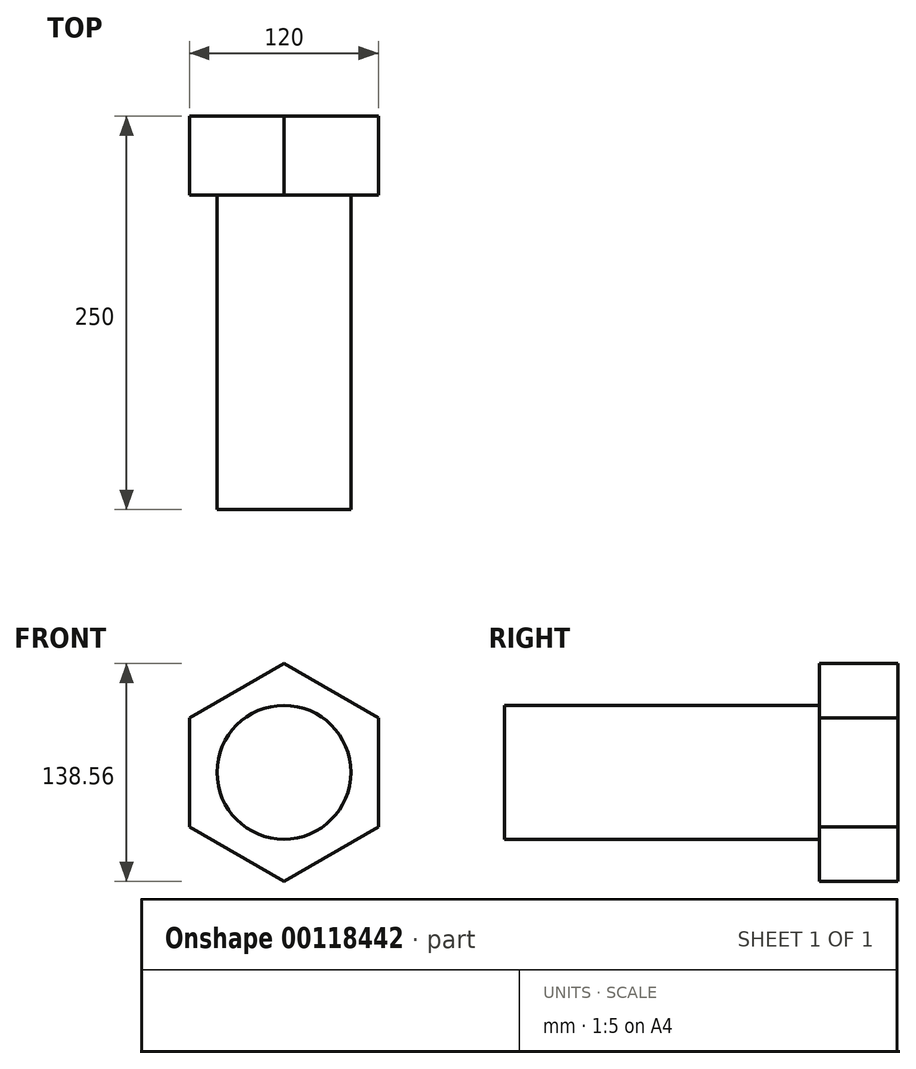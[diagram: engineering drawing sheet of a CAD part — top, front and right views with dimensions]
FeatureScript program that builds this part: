
annotation { "Feature Type Name" : "Feature", "Feature Type Description" : "" }
export const myFeature = defineFeature(function(context is Context, id is Id, definition is map)
    precondition{}
    {
        {
            var Q0;
            Q0=qCreatedBy(makeId("Front.planeOp"),FACE);
            var sketch = newSketch(context, id + "F0", { "sketchPlane" : qUnion([Q0])});
            skCircle(sketch, "E0.cCircle", {"center": v(0, 0) * mm, "radius": 60 * mm, "construction": true});
            skLineSegment(sketch, "E0.0", {"start": v(-60, -34.64) * mm, "end": v(-60, 34.64) * mm});
            skLineSegment(sketch, "E0.1", {"start": v(-60, 34.64) * mm, "end": v(0, 69.28) * mm});
            skLineSegment(sketch, "E0.2", {"start": v(0, 69.28) * mm, "end": v(60, 34.64) * mm});
            skLineSegment(sketch, "E0.3", {"start": v(60, 34.64) * mm, "end": v(60, -34.64) * mm});
            skLineSegment(sketch, "E0.4", {"start": v(60, -34.64) * mm, "end": v(0, -69.28) * mm});
            skLineSegment(sketch, "E0.5", {"start": v(0, -69.28) * mm, "end": v(-60, -34.64) * mm});
            skPoint(sketch, "E0.0.midPoint", {"position": v(-60, 0) * mm});
            skSolve(sketch);
        }
        {
            var Q0;
            Q0 = qSketchRegion(id + "F0", true);
            extrude(context, id + "F1", {"entities" : qUnion([Q0]), "endBound" : BoundingType.SYMMETRIC, "depth" : 50 * mm});
        }
        {
            var Q0;
            Q0=makeQuery(id+"F1.opExtrude","CAP_FACE",FACE,{"disambiguationData":[OSD([sQuery(id+"F0.wireOp",EDGE,"E0.0"),sQuery(id+"F0.wireOp",EDGE,"E0.1"),sQuery(id+"F0.wireOp",EDGE,"E0.2"),sQuery(id+"F0.wireOp",EDGE,"E0.3"),sQuery(id+"F0.wireOp",EDGE,"E0.4"),sQuery(id+"F0.wireOp",EDGE,"E0.5")])],"isStart":false});
            var sketch = newSketch(context, id + "F2", { "sketchPlane" : qUnion([Q0])});
            skCircle(sketch, "E1", {"center": v(0, 0) * mm, "radius": 42.5 * mm});
            skSolve(sketch);
        }
        {
            var Q0;
            Q0=makeQuery(id+"F2.imprint","IMPRINT",FACE,{"disambiguationData":[TD([[makeQuery(id+"F2.imprint","IMPRINT",EDGE,{"derivedFrom":sQuery(id+"F2.wireOp",EDGE,"E1")}),1.0]])]});
            extrude(context, id + "F3", {"entities" : qUnion([Q0]), "operationType" : NewBodyOperationType.ADD, "depth" : 200 * mm});
        }
    });
